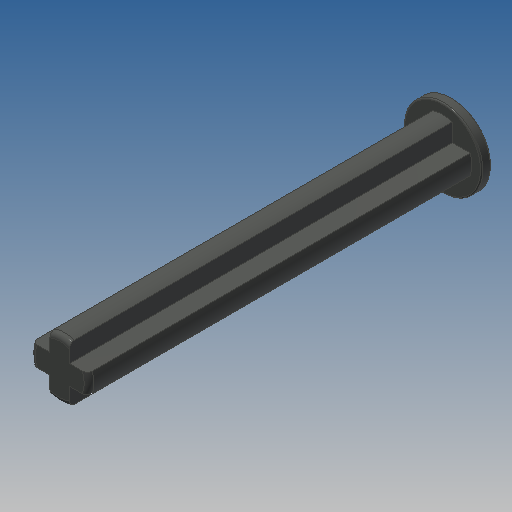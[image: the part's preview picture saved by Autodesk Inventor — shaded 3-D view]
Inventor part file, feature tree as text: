
AUTODESK INVENTOR PART (.ipt)
format: ipt  version: 2022.2 (Build 262287000, 287)  size: 177,152 bytes
history: native  units: in
note: dims shown in document units (in); Inventor stores cm internally (conversion verified against a paired STEP export)
features: extrude x2, sketch x2, fillet x1
ambient origin geometry x8: Origin, YZ Plane, XZ Plane, XY Plane, X Axis, Y Axis, Z Axis, Center Point
bodies: Solid1 (feature_tree)
feature tree (5):
  extrude  "Extrusion1"  Depth=0.063in
  extrude  "Extrusion2"  TaperAngle=0.0deg  [1 undecoded]
  fillet  "Fillet1"  Radius=0.0157in
  sketch  "Sketch1"  dims[d0=0.189in d1=0.063in]
  sketch  "Sketch2"  dims[d2=1.2598in d3=0.0in d4=0.0157in d7=0.252in d8=0.0315in d9=0.0in d10=0.0039in d11=0.0in d12=0.0in]
note: 1 required parameter value undecoded (feature->parameter linkage not recoverable at this tier; creation-order binding heuristic only, values carry confidence <= 0.55)
